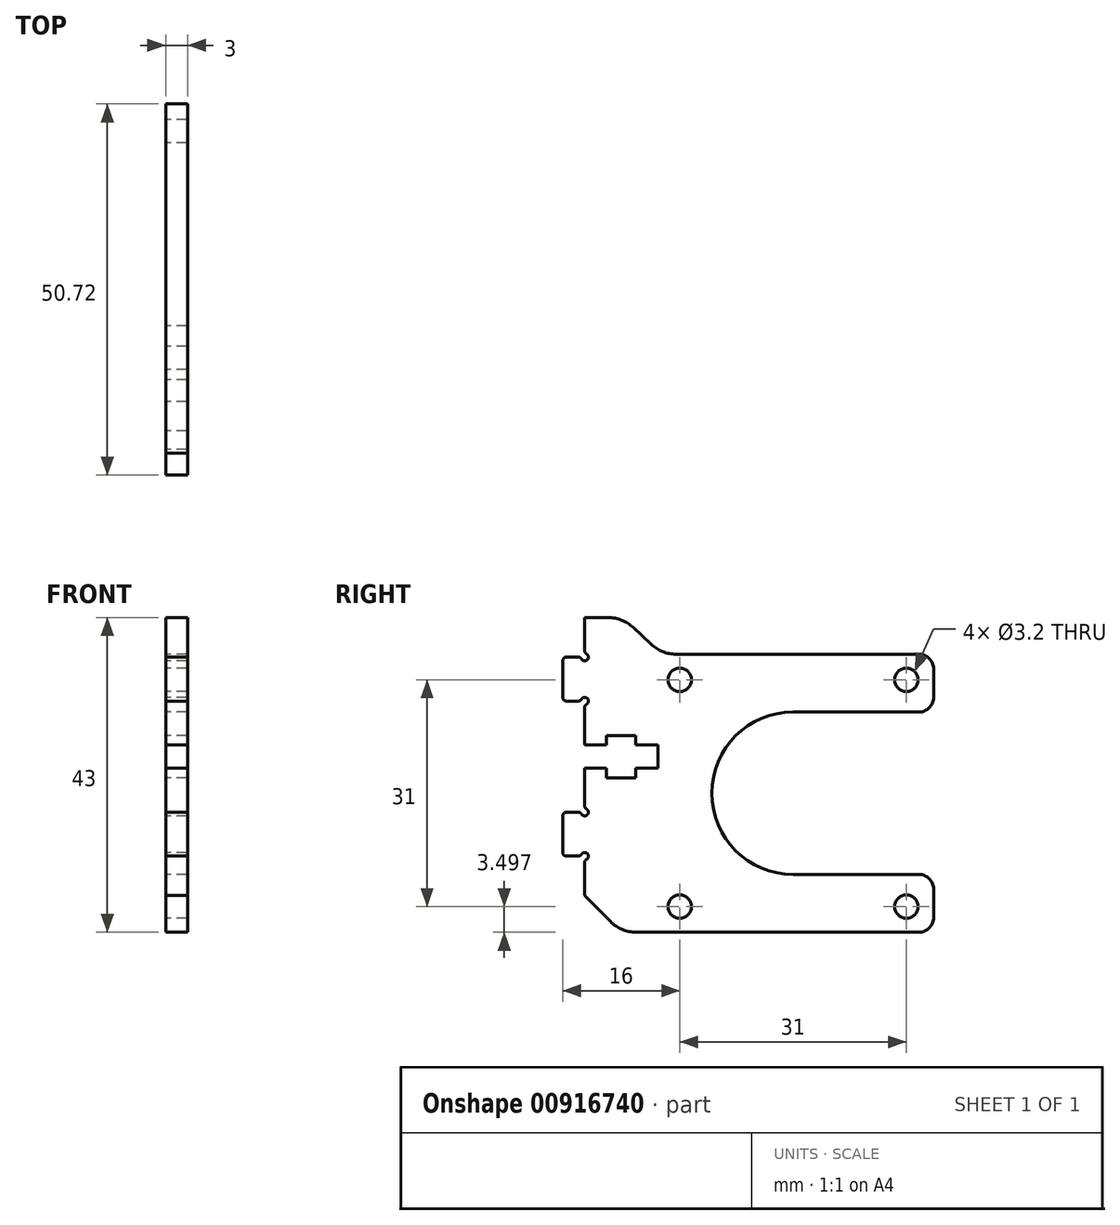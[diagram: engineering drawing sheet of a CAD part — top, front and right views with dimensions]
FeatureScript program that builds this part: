
annotation { "Feature Type Name" : "Feature", "Feature Type Description" : "" }
export const myFeature = defineFeature(function(context is Context, id is Id, definition is map)
    precondition{}
    {
        {
            var Q0;
            Q0=qCreatedBy(makeId("Right.planeOp"),FACE);
            var sketch = newSketch(context, id + "F0", { "sketchPlane" : qUnion([Q0])});
            skLineSegment(sketch, "E0", {"start": v(6.5, 20.93) * mm, "end": v(6.5, 24.13) * mm});
            skLineSegment(sketch, "E1", {"start": v(6.5, 24.13) * mm, "end": v(3.5, 24.13) * mm});
            skLineSegment(sketch, "E2", {"start": v(3.5, 24.13) * mm, "end": v(3.5, 25.4) * mm});
            skLineSegment(sketch, "E3", {"start": v(3.5, 25.4) * mm, "end": v(-0.5, 25.4) * mm});
            skLineSegment(sketch, "E4", {"start": v(-0.5, 25.4) * mm, "end": v(-0.5, 24.13) * mm});
            skLineSegment(sketch, "E5", {"start": v(-0.5, 24.13) * mm, "end": v(-3.5, 24.13) * mm});
            skLineSegment(sketch, "E6", {"start": v(-3.5, 24.13) * mm, "end": v(-3.5, 29.26) * mm});
            skArc(sketch, "E7", {"start": v(-3.26, 29.7) * mm, "mid": v(-3.44, 29.51) * mm, "end": v(-3.5, 29.26) * mm});
            skArc(sketch, "E8", {"start": v(-3.26, 29.7) * mm, "mid": v(-3.16, 30.48) * mm, "end": v(-3.94, 30.38) * mm});
            skArc(sketch, "E9", {"start": v(-4.38, 30.13) * mm, "mid": v(-4.13, 30.2) * mm, "end": v(-3.94, 30.38) * mm});
            skLineSegment(sketch, "E10", {"start": v(-4.38, 30.13) * mm, "end": v(-6, 30.13) * mm});
            skArc(sketch, "E11", {"start": v(-6.5, 30.63) * mm, "mid": v(-6.36, 30.27) * mm, "end": v(-6, 30.13) * mm});
            skLineSegment(sketch, "E12", {"start": v(-6.5, 30.63) * mm, "end": v(-6.5, 35.63) * mm});
            skArc(sketch, "E13", {"start": v(-6, 36.13) * mm, "mid": v(-6.36, 35.98) * mm, "end": v(-6.5, 35.63) * mm});
            skLineSegment(sketch, "E14", {"start": v(-6, 36.13) * mm, "end": v(-4.38, 36.13) * mm});
            skArc(sketch, "E15", {"start": v(-3.94, 35.88) * mm, "mid": v(-4.13, 36.06) * mm, "end": v(-4.38, 36.13) * mm});
            skArc(sketch, "E16", {"start": v(-3.94, 35.88) * mm, "mid": v(-3.16, 35.77) * mm, "end": v(-3.26, 36.56) * mm});
            skArc(sketch, "E17", {"start": v(-3.5, 37) * mm, "mid": v(-3.44, 36.74) * mm, "end": v(-3.26, 36.56) * mm});
            skLineSegment(sketch, "E18", {"start": v(-3.5, 37) * mm, "end": v(-3.5, 41.53) * mm});
            skArc(sketch, "E19", {"start": v(-3.26, 8.5) * mm, "mid": v(-3.44, 8.31) * mm, "end": v(-3.5, 8.06) * mm});
            skArc(sketch, "E20", {"start": v(-3.26, 8.5) * mm, "mid": v(-3.16, 9.28) * mm, "end": v(-3.94, 9.18) * mm});
            skArc(sketch, "E21", {"start": v(-4.38, 8.93) * mm, "mid": v(-4.13, 9) * mm, "end": v(-3.94, 9.18) * mm});
            skLineSegment(sketch, "E22", {"start": v(-4.38, 8.93) * mm, "end": v(-6, 8.93) * mm});
            skArc(sketch, "E23", {"start": v(-6.5, 9.43) * mm, "mid": v(-6.36, 9.07) * mm, "end": v(-6, 8.93) * mm});
            skLineSegment(sketch, "E24", {"start": v(-6.5, 9.43) * mm, "end": v(-6.5, 14.43) * mm});
            skArc(sketch, "E25", {"start": v(-6, 14.93) * mm, "mid": v(-6.36, 14.78) * mm, "end": v(-6.5, 14.43) * mm});
            skLineSegment(sketch, "E26", {"start": v(-6, 14.93) * mm, "end": v(-4.38, 14.93) * mm});
            skArc(sketch, "E27", {"start": v(-3.94, 14.68) * mm, "mid": v(-4.13, 14.86) * mm, "end": v(-4.38, 14.93) * mm});
            skArc(sketch, "E28", {"start": v(-3.94, 14.68) * mm, "mid": v(-3.16, 14.57) * mm, "end": v(-3.26, 15.36) * mm});
            skArc(sketch, "E29", {"start": v(-3.5, 15.8) * mm, "mid": v(-3.44, 15.54) * mm, "end": v(-3.26, 15.36) * mm});
            skLineSegment(sketch, "E30", {"start": v(-3.5, 15.8) * mm, "end": v(-3.5, 20.93) * mm});
            skLineSegment(sketch, "E31", {"start": v(-3.5, 20.93) * mm, "end": v(-0.5, 20.93) * mm});
            skLineSegment(sketch, "E32", {"start": v(-0.5, 20.93) * mm, "end": v(-0.5, 19.65) * mm});
            skLineSegment(sketch, "E33", {"start": v(-0.5, 19.65) * mm, "end": v(3.5, 19.65) * mm});
            skLineSegment(sketch, "E34", {"start": v(3.5, 19.65) * mm, "end": v(3.5, 20.93) * mm});
            skLineSegment(sketch, "E35", {"start": v(3.5, 20.93) * mm, "end": v(6.5, 20.93) * mm});
            skLineSegment(sketch, "E36", {"start": v(-3.5, 3.53) * mm, "end": v(-3.5, 8.06) * mm});
            skLineSegment(sketch, "E37", {"start": v(-3.5, 41.53) * mm, "end": v(-0.3, 41.53) * mm});
            skArc(sketch, "E38", {"start": v(3.14, 40.17) * mm, "mid": v(1.55, 41.17) * mm, "end": v(-0.3, 41.53) * mm});
            skLineSegment(sketch, "E39", {"start": v(3.14, 40.17) * mm, "end": v(5.56, 37.89) * mm});
            skArc(sketch, "E40", {"start": v(5.56, 37.89) * mm, "mid": v(7.14, 36.88) * mm, "end": v(8.99, 36.53) * mm});
            skLineSegment(sketch, "E41", {"start": v(-3.5, 3.53) * mm, "end": v(0, 0) * mm});
            skArc(sketch, "E42", {"start": v(0, 0) * mm, "mid": v(1.63, -1.1) * mm, "end": v(3.54, -1.47) * mm});
            skCircle(sketch, "E43", {"center": v(9.5, 2.03) * mm, "radius": 1.6 * mm});
            skCircle(sketch, "E44", {"center": v(40.5, 2.03) * mm, "radius": 1.6 * mm});
            skCircle(sketch, "E45", {"center": v(9.5, 33.03) * mm, "radius": 1.6 * mm});
            skCircle(sketch, "E46", {"center": v(40.5, 33.03) * mm, "radius": 1.6 * mm});
            skArc(sketch, "E47", {"start": v(25, 28.63) * mm, "mid": v(13.9, 17.53) * mm, "end": v(25, 6.43) * mm});
            skArc(sketch, "E48", {"start": v(44.2, 34.53) * mm, "mid": v(43.62, 35.94) * mm, "end": v(42.2, 36.53) * mm});
            skArc(sketch, "E49", {"start": v(42.2, -1.47) * mm, "mid": v(43.62, -0.89) * mm, "end": v(44.2, 0.53) * mm});
            skLineSegment(sketch, "E50", {"start": v(25, 28.63) * mm, "end": v(42.2, 28.63) * mm});
            skLineSegment(sketch, "E51", {"start": v(44.2, 34.53) * mm, "end": v(44.2, 30.63) * mm});
            skArc(sketch, "E52", {"start": v(42.2, 28.63) * mm, "mid": v(43.62, 29.21) * mm, "end": v(44.2, 30.63) * mm});
            skLineSegment(sketch, "E53", {"start": v(25, 6.43) * mm, "end": v(42.2, 6.43) * mm});
            skLineSegment(sketch, "E54", {"start": v(44.2, 4.43) * mm, "end": v(44.2, 0.53) * mm});
            skArc(sketch, "E55", {"start": v(44.2, 4.43) * mm, "mid": v(43.62, 5.84) * mm, "end": v(42.2, 6.43) * mm});
            skLineSegment(sketch, "E56", {"start": v(3.54, -1.47) * mm, "end": v(42.2, -1.47) * mm});
            skLineSegment(sketch, "E57", {"start": v(42.2, 36.53) * mm, "end": v(8.99, 36.53) * mm});
            skSolve(sketch);
        }
        {
            var Q0;
            Q0=makeQuery(id+"F0.imprint","IMPRINT",FACE,{"disambiguationData":[TD([[makeQuery(id+"F0.imprint","IMPRINT",EDGE,{"derivedFrom":sQuery(id+"F0.wireOp",EDGE,"E0")}),-1.0]])]});
            extrude(context, id + "F1", {"entities" : qUnion([Q0]), "depth" : 3 * mm, "offsetDistance" : 25 * mm});
        }
    });
